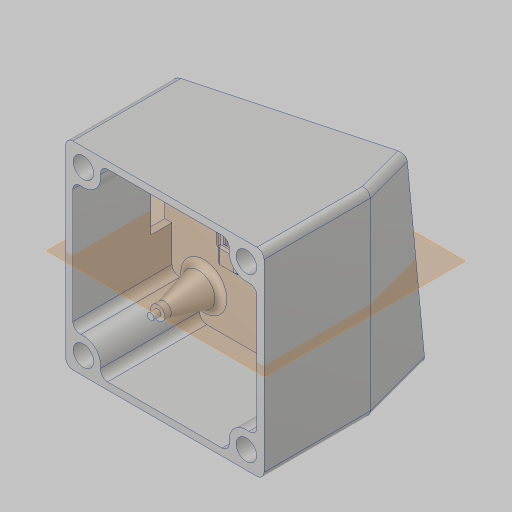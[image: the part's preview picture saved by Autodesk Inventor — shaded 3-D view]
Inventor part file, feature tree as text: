
AUTODESK INVENTOR PART (.ipt)
format: ipt  version: 2023.5 (Build 275446000, 446)  size: 373,760 bytes
history: native  units: in
note: dims shown in document units (in); Inventor stores cm internally (conversion verified against a paired STEP export)
features: extrude x8, projected_geometry x4, hole x2, fillet x2, chamfer x2, mirror x1, shell x1, plane x1, draft x1, sketch x1
ambient origin geometry x8: Origin, YZ Plane, XZ Plane, XY Plane, X Axis, Y Axis, Z Axis, Center Point
bodies: Solid1 (feature_tree)
feature tree (23):
  extrude  "Extrusion1"  Depth=0.2362in
  hole  "Hole1"  [1 undecoded]
  extrude  "Extrusion6"  Depth=0.2362in
  mirror  "Mirror1"
  shell  "Shell1"  Thickness=1.1811in
  extrude  "Extrusion7"  Depth=0.0787in
  fillet  "Fillet1"  Radius=0.3937in
  extrude  "Extrusion2"  Depth=0.2362in
  chamfer  "Chamfer1"  Distance=0.0787in
  extrude  "Extrusion3"  Depth=0.2362in
  extrude  "Extrusion4"  Depth=0.2362in
  plane  "Work Plane1"
  extrude  "Extrusion5"  Depth=0.2362in
  chamfer  "Chamfer2"  Distance=0.1575in
  fillet  "Fillet3"  Radius=0.5906in
  extrude  "Extrusion8"  Depth=0.0787in TaperAngle=75.0deg
  draft  "FaceDraft1"
  hole  "Hole3"  [1 undecoded]
  projected_geometry  "Projected Loop1"
  projected_geometry  "Projected Loop2"
  projected_geometry  "Projected Loop3"
  sketch  "Sketch12"  dims[d0=1.4961in d1=1.4961in d2=1.3386in d3=1.3386in d5=1.1811in d6=0.0in d7=0.0787in d8=0.3937in d9=1.811in d10=0.2283in d11=0.2362in d12=0.385in d13=0.0787in d14=0.5635in d15=0.315in d16=0.8108in d17=0.0787in d18=0.1575in d19=0.1575in d20=0.1575in d21=0.1575in d22=0.5906in d23=0.0in d24=0.1181in d25=0.0787in d26=75.0deg d27=0.0748in d28=0.0748in d29=0.0748in d30=0.0748in d31=0.0787in d32=0.0in d33=0.4724in d34=0.2362in d35=0.0787in d36=1.1811in d37=0.0in d42=0.1969in d43=0.0in d44=0.0197in d45=0.0787in d46=0.481in d47=0.2283in d48=0.2283in d49=0.1969in d50=1.0in d51=0.2756in d52=0.0in d61=0.0787in d62=15.0deg d63=0.3937in d64=0.0in d65=0.0591in d66=0.1969in d67=0.5906in d68=45.0deg d69=45.0deg d70=0.5906in d71=0.1843in d72=0.0591in d73=0.0591in d74=1.5748in d75=1.5748in d76=0.2283in d77=0.2283in d80=0.315in d81=0.0in d82=0.2283in d83=0.0515in d86=0.2283in d87=0.2362in d88=0.385in d89=0.0787in d90=0.5635in d91=0.2362in d92=0.0in d93=0.5in d94=1.5in d96=0.375in d60=0.0in]
  projected_geometry  "Project Cut Edges1"
note: 2 required parameter values undecoded (feature->parameter linkage not recoverable at this tier; creation-order binding heuristic only, values carry confidence <= 0.55)
